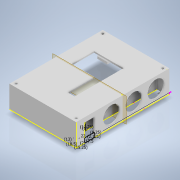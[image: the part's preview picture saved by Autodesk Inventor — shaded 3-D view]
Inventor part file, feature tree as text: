
AUTODESK INVENTOR PART (.ipt)
format: ipt  version: 2020.1 (Build 241239000, 239)  size: 658,944 bytes
history: native  units: mm
features: sketch x35, extrude x21, chamfer x2, hole x2, mirror x2, projected_geometry x2, plane x1
ambient origin geometry x8: Origin, YZ Plane, XZ Plane, XY Plane, X Axis, Y Axis, Z Axis, Center Point
bodies: Solid1 (feature_tree)
feature tree (65):
  extrude  "Extrusion1"  Depth=160.0mm
  extrude  "Extrusion2"  Depth=40.0mm
  sketch  "Sketch3"  dims[d2=40.0mm d3=0.0mm d4=60.0mm]
  extrude  "Extrusion3"  Depth=40.0mm
  extrude  "Extrusion4"  Depth=30.0mm
  sketch  "Sketch6"  dims[d9=30.0mm d10=30.0mm]
  extrude  "Extrusion5"  Depth=30.0mm
  extrude  "Extrusion10"  Depth=23.5mm
  sketch  "Sketch13"  dims[d18=160.0mm d19=2.4mm d20=0.0mm]
  extrude  "Extrusion11"  Depth=120.0mm
  sketch  "Sketch15"  dims[d26=25.0mm d27=23.0mm]
  extrude  "Extrusion12"  Depth=2.4mm TaperAngle=0.0deg
  sketch  "Sketch18"  dims[d45=4.0mm d46=0.0mm d47=5.0mm]
  sketch  "Sketch22"  dims[d48=160.0mm d49=36.0mm d50=0.0mm]
  extrude  "Extrusion17"  Depth=20.5mm
  sketch  "Sketch28"  dims[d69=49.0mm d70=3.5mm]
  sketch  "Sketch30"  dims[d71=20.0mm d72=6.0mm]
  sketch  "Sketch31"  dims[d73=6.0mm d74=6.0mm]
  extrude  "Extrusion21"  Depth=23.0mm
  sketch  "Sketch33"  dims[d75=6.0mm d76=8.0mm d77=0.0mm]
  sketch  "Sketch34"  dims[d78=2.75mm d79=2.75mm]
  extrude  "Extrusion30"  Depth=4.0mm TaperAngle=0.0deg
  extrude  "Extrusion31"  Depth=4.0mm
  extrude  "Extrusion32"  Depth=160.0mm TaperAngle=0.0deg
  extrude  "Extrusion33"  Depth=58.0mm
  sketch  "Sketch46"  dims[d103=4.0mm]
  extrude  "Extrusion34"  Depth=3.5mm
  extrude  "Extrusion35"  Depth=6.0mm
  sketch  "Sketch49"  dims[d129=1.0mm d158=1.5mm]
  extrude  "Extrusion36"  Depth=6.0mm
  plane  "Work Plane3"
  sketch  "Sketch52"  dims[d162=22.0mm]
  extrude  "Extrusion38"  Depth=6.0mm TaperAngle=0.0deg
  extrude  "Extrusion40"  Depth=2.75mm
  sketch  "Sketch56"  dims[d165=22.0mm d166=10.0mm d167=0.0mm]
  extrude  "Extrusion41"  Depth=2.75mm
  chamfer  "Chamfer2"  Distance=10.0mm
  sketch  "Sketch57"  dims[d168=8.05mm d169=1.6mm]
  hole  "Hole1"  [1 undecoded]
  mirror  "Mirror5"
  extrude  "Extrusion42"  Depth=1.5mm
  chamfer  "Chamfer3"  Distance=10.0mm
  hole  "Hole2"  [1 undecoded]
  mirror  "Mirror6"
  sketch  "Sketch2"  dims[d0=2.0mm d1=160.0mm]
  sketch  "Sketch4"  dims[d5=20.0mm d6=40.0mm]
  sketch  "Sketch5"  dims[d7=20.0mm d8=30.0mm]
  sketch  "Sketch7"  dims[d11=17.5mm d12=23.5mm]
  sketch  "Sketch12"  dims[d13=40.0mm d14=0.0mm d17=120.0mm]
  sketch  "Sketch14"  dims[d21=28.6mm d22=0.0mm d25=20.5mm]
  sketch  "Sketch16"  dims[d29=1.5mm d30=0.0mm d43=4.0mm d44=0.0mm]
  sketch  "Sketch23"  dims[d67=58.0mm d68=58.0mm]
  projected_geometry  "Projected Loop2"
  sketch  "Sketch42"  dims[d80=2.75mm d81=2.75mm]
  sketch  "Sketch43"  dims[d96=120.0mm]
  sketch  "Sketch44"  dims[d101=6.0mm]
  sketch  "Sketch45"  dims[d102=4.0mm]
  sketch  "Sketch47"  dims[d104=4.0mm]
  sketch  "Sketch48"  dims[d105=4.0mm d106=10.0mm d107=0.0mm]
  sketch  "Sketch50"  dims[d159=1.5mm d160=1.5mm]
  sketch  "Sketch53"  dims[d163=4.35mm]
  projected_geometry  "Projected Loop4"
  sketch  "Sketch55"  dims[d164=9.0mm]
  sketch  "Sketch58"  dims[d170=3.4mm]
  sketch  "Sketch59"  dims[d172=2.0mm d173=3.25mm d174=1.25mm d175=30.0mm d176=0.0mm d177=1.0mm d178=0.0mm d179=30.0mm d180=0.0mm d181=17.5mm d182=30.0mm d183=0.0mm d184=8.25mm d185=15.25mm d186=2.0mm d191=8.25mm d192=0.0mm d193=11.25mm d194=22.0mm d195=5.0mm d196=0.0mm d197=5.0mm d198=13.0mm d199=18.5mm d200=2.65mm d201=8.0mm d202=2.65mm d203=8.0mm d204=11.25mm d205=0.0mm d210=2.12132mm d211=1.5mm d212=10.0mm d213=0.0mm d225=40.0mm d226=53.0mm d227=41.0mm d228=25.419mm d229=12.0mm d230=39.0mm d231=10.0mm d232=0.0mm d233=0.0mm d235=1.2mm d236=6.0mm d237=4.0mm d238=18.0mm d239=10.0mm d240=10.0mm d241=0.0mm d242=6.0mm d243=2.0mm d244=45.0deg d245=4.0mm d246=6.0mm d247=8.4mm d248=2.0mm d249=90.0deg d250=10.0mm d251=20.594885mm d252=12.0mm d253=10.0mm d254=10.0mm d255=0.0mm d256=10.0mm d257=2.0mm d258=45.0deg d259=6.0mm d260=6.0mm d261=4.0mm d262=6.0mm d263=8.4mm d264=2.0mm d265=90.0deg d266=10.0mm d267=20.594885mm d15=0.5mm d16=0.872665mm d28=0.872665mm d35=0.5mm d36=0.872665mm d37=0.5mm d38=0.872665mm d83=0.5mm d84=0.872665mm d85=0.5mm d86=0.872665mm d98=0.5mm d99=0.872665mm d100=0.5mm d126=0.5mm d127=0.872665mm d128=0.5mm d148=0.5mm d149=0.872665mm d150=0.5mm d151=0.872665mm d152=0.5mm d153=0.872665mm d154=0.5mm d155=0.872665mm d268=0.75mm d269=20.594885mm d270=0.0625mm d271=0.75mm d272=0.375mm]
note: 2 required parameter values undecoded (feature->parameter linkage not recoverable at this tier; creation-order binding heuristic only, values carry confidence <= 0.55)
